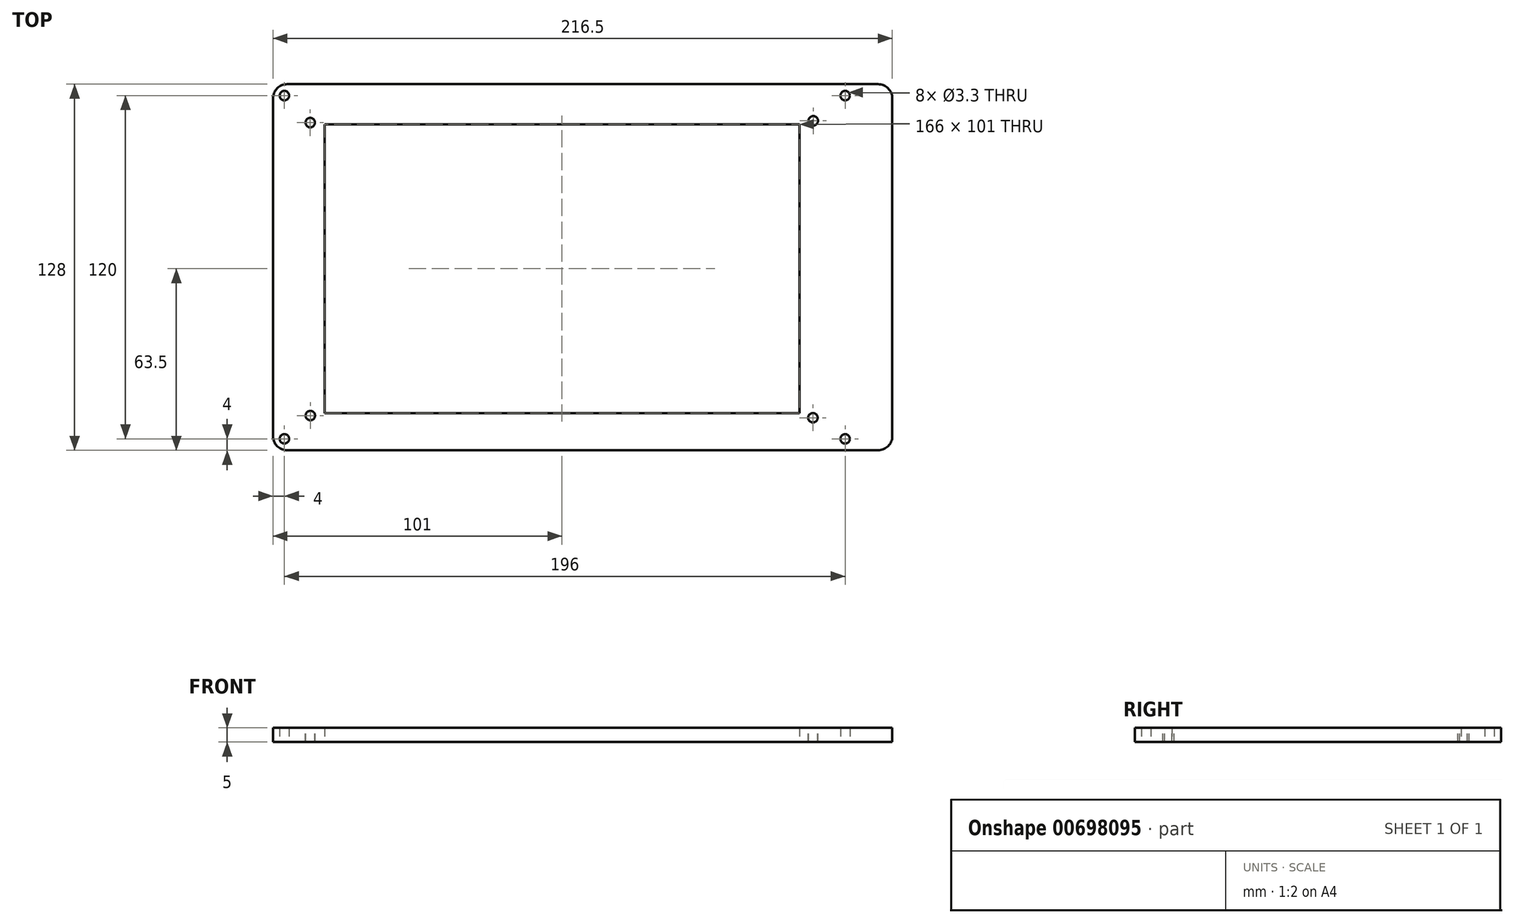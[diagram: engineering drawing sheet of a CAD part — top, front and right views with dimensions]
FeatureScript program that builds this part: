
annotation { "Feature Type Name" : "Feature", "Feature Type Description" : "" }
export const myFeature = defineFeature(function(context is Context, id is Id, definition is map)
    precondition{}
    {
        {
            var Q0;
            Q0=qCreatedBy(makeId("Top.planeOp"),FACE);
            var sketch = newSketch(context, id + "F0", { "sketchPlane" : qUnion([Q0])});
            skLineSegment(sketch, "E0.bottom", {"start": v(83, 50.5) * mm, "end": v(-83, 50.5) * mm});
            skLineSegment(sketch, "E0.top", {"start": v(83, -50.5) * mm, "end": v(-83, -50.5) * mm});
            skLineSegment(sketch, "E0.left", {"start": v(83, 50.5) * mm, "end": v(83, -50.5) * mm});
            skLineSegment(sketch, "E0.right", {"start": v(-83, 50.5) * mm, "end": v(-83, -50.5) * mm});
            skPoint(sketch, "E0.middle", {"position": v(0, 0) * mm});
            skLineSegment(sketch, "E1.0", {"start": v(-91, 54.5) * mm, "end": v(-91, -53.5) * mm, "construction": true});
            skLineSegment(sketch, "E1.1", {"start": v(93, 54.5) * mm, "end": v(-91, 54.5) * mm, "construction": true});
            skLineSegment(sketch, "E1.2", {"start": v(93, 54.5) * mm, "end": v(93, -53.5) * mm, "construction": true});
            skLineSegment(sketch, "E1.3", {"start": v(93, -53.5) * mm, "end": v(-91, -53.5) * mm, "construction": true});
            skLineSegment(sketch, "E2.0", {"start": v(103, 64.5) * mm, "end": v(-101, 64.5) * mm});
            skLineSegment(sketch, "E2.1", {"start": v(103, 64.5) * mm, "end": v(103, -63.5) * mm});
            skLineSegment(sketch, "E2.2", {"start": v(103, -63.5) * mm, "end": v(-101, -63.5) * mm});
            skLineSegment(sketch, "E2.3", {"start": v(-101, 64.5) * mm, "end": v(-101, -63.5) * mm});
            skLineSegment(sketch, "E3.0", {"start": v(99, 60.5) * mm, "end": v(-97, 60.5) * mm, "construction": true});
            skLineSegment(sketch, "E3.1", {"start": v(99, 60.5) * mm, "end": v(99, -59.5) * mm, "construction": true});
            skLineSegment(sketch, "E3.2", {"start": v(99, -59.5) * mm, "end": v(-97, -59.5) * mm, "construction": true});
            skLineSegment(sketch, "E3.3", {"start": v(-97, 60.5) * mm, "end": v(-97, -59.5) * mm, "construction": true});
            skLineSegment(sketch, "E4", {"start": v(103, 64.5) * mm, "end": v(115.5, 64.5) * mm});
            skLineSegment(sketch, "E5", {"start": v(115.5, -63.5) * mm, "end": v(103, -63.5) * mm});
            skLineSegment(sketch, "E6", {"start": v(115.5, 64.5) * mm, "end": v(115.5, -63.5) * mm});
            skPoint(sketch, "E7.orphan", {"position": v(133, -63.5) * mm});
            skSolve(sketch);
        }
        {
            var Q0;
            Q0=makeQuery(id+"F0.imprint","IMPRINT",FACE,{"disambiguationData":[TD([[makeQuery(id+"F0.imprint","IMPRINT",EDGE,{"derivedFrom":sQuery(id+"F0.wireOp",EDGE,"E0.bottom")}),-1.0]])]});
            var Q1;
            Q1=makeQuery(id+"F0.imprint","IMPRINT",FACE,{"disambiguationData":[TD([[makeQuery(id+"F0.imprint","IMPRINT",EDGE,{"derivedFrom":sQuery(id+"F0.wireOp",EDGE,"E2.1")}),1.0]])]});
            extrude(context, id + "F1", {"entities" : qUnion([Q0, Q1]), "depth" : 5 * mm, "offsetDistance" : 25 * mm});
        }
        {
            var Q0;
            Q0=sQuery(id+"F0.wireOp",VERTEX,"E3.0.end");
            var Q1;
            Q1=sQuery(id+"F0.wireOp",VERTEX,"E3.0.start");
            var Q2;
            Q2=sQuery(id+"F0.wireOp",VERTEX,"E3.1.end");
            var Q3;
            Q3=sQuery(id+"F0.wireOp",VERTEX,"E3.2.end");
            var Q4;
            Q4=makeQuery(id+"F1.opExtrude","SWEPT_BODY",BODY,{"disambiguationData":[OSD([sQuery(id+"F0.wireOp",EDGE,"E0.bottom"),sQuery(id+"F0.wireOp",EDGE,"E0.top"),sQuery(id+"F0.wireOp",EDGE,"E0.left"),sQuery(id+"F0.wireOp",EDGE,"E0.right"),sQuery(id+"F0.wireOp",EDGE,"E2.0"),sQuery(id+"F0.wireOp",EDGE,"E2.1"),sQuery(id+"F0.wireOp",EDGE,"E2.2"),sQuery(id+"F0.wireOp",EDGE,"E2.3")])]});
            hole(context, id + "F2", {"style" : HoleStyle.SIMPLE, "endStyle" : HoleEndStyle.THROUGH, "oppositeDirection" : true, "standardTappedOrClearance" : lookupTablePath({ "standard" : "ISO", "fit" : "Normal", "size" : "M3", "type" : "Clearance" }), "standardBlindInLast" : lookupTablePath({ "fit" : "Standard", "standard" : "ISO", "size" : "M3", "type" : "Clearance" }), "holeDiameter" : 3.3 * mm, "majorDiameter" : 5 * mm, "isTappedThrough" : true, "tappedDepth" : 12 * mm, "tapClearance" : 3, "startFromSketch" : true, "locations" : qUnion([Q0, Q1, Q2, Q3]), "scope" : qUnion([Q4])});
        }
        {
            var Q0;
            Q0=makeQuery(id+"F1.opExtrude","CAP_FACE",FACE,{"disambiguationData":[OSD([sQuery(id+"F0.wireOp",EDGE,"E0.bottom"),sQuery(id+"F0.wireOp",EDGE,"E0.top"),sQuery(id+"F0.wireOp",EDGE,"E0.left"),sQuery(id+"F0.wireOp",EDGE,"E0.right"),sQuery(id+"F0.wireOp",EDGE,"E2.0"),sQuery(id+"F0.wireOp",EDGE,"E2.2"),sQuery(id+"F0.wireOp",EDGE,"E2.3"),sQuery(id+"F0.wireOp",EDGE,"E4"),sQuery(id+"F0.wireOp",EDGE,"E5"),sQuery(id+"F0.wireOp",EDGE,"E6")])],"isStart":false});
            var sketch = newSketch(context, id + "F3", { "sketchPlane" : qUnion([Q0])});
            skPoint(sketch, "E8", {"position": v(87.73, -52.12) * mm});
            skPoint(sketch, "E9", {"position": v(-87.92, -51.37) * mm});
            skPoint(sketch, "E10", {"position": v(-87.97, 51.06) * mm});
            skPoint(sketch, "E11", {"position": v(87.85, 51.7) * mm});
            skSolve(sketch);
        }
        {
            var Q0;
            Q0=sQuery(id+"F3.wireOp",VERTEX,"E10");
            var Q1;
            Q1=sQuery(id+"F3.wireOp",VERTEX,"E11");
            var Q2;
            Q2=sQuery(id+"F3.wireOp",VERTEX,"E8");
            var Q3;
            Q3=sQuery(id+"F3.wireOp",VERTEX,"E9");
            var Q4;
            Q4=makeQuery(id+"F1.opExtrude","SWEPT_BODY",BODY,{"disambiguationData":[OSD([sQuery(id+"F0.wireOp",EDGE,"E0.bottom"),sQuery(id+"F0.wireOp",EDGE,"E0.top"),sQuery(id+"F0.wireOp",EDGE,"E0.left"),sQuery(id+"F0.wireOp",EDGE,"E0.right"),sQuery(id+"F0.wireOp",EDGE,"E2.0"),sQuery(id+"F0.wireOp",EDGE,"E2.2"),sQuery(id+"F0.wireOp",EDGE,"E2.3"),sQuery(id+"F0.wireOp",EDGE,"E4"),sQuery(id+"F0.wireOp",EDGE,"E5"),sQuery(id+"F0.wireOp",EDGE,"E6")])]});
            hole(context, id + "F4", {"style" : HoleStyle.SIMPLE, "endStyle" : HoleEndStyle.THROUGH, "standardTappedOrClearance" : lookupTablePath({ "standard" : "ISO", "fit" : "Normal", "size" : "M3", "type" : "Clearance" }), "standardBlindInLast" : lookupTablePath({ "fit" : "Standard", "standard" : "ISO", "size" : "M3", "type" : "Clearance" }), "holeDiameter" : 3.3 * mm, "majorDiameter" : 5 * mm, "isTappedThrough" : true, "tappedDepth" : 12 * mm, "tapClearance" : 3, "locations" : qUnion([Q0, Q1, Q2, Q3]), "scope" : qUnion([Q4])});
        }
        {
            var Q0;
            Q0=makeQuery(id+"F1.opExtrude","SWEPT_EDGE",EDGE,{"disambiguationData":[OSD([sQuery(id+"F0.wireOp",EDGE,"E2.0"),sQuery(id+"F0.wireOp",EDGE,"E2.3")])]});
            var Q1;
            Q1=makeQuery(id+"F1.opExtrude","SWEPT_EDGE",EDGE,{"disambiguationData":[OSD([sQuery(id+"F0.wireOp",EDGE,"E4"),sQuery(id+"F0.wireOp",EDGE,"E6")])]});
            var Q2;
            Q2=makeQuery(id+"F1.opExtrude","SWEPT_EDGE",EDGE,{"disambiguationData":[OSD([sQuery(id+"F0.wireOp",EDGE,"E5"),sQuery(id+"F0.wireOp",EDGE,"E6")])]});
            var Q3;
            Q3=makeQuery(id+"F1.opExtrude","SWEPT_EDGE",EDGE,{"disambiguationData":[OSD([sQuery(id+"F0.wireOp",EDGE,"E2.2"),sQuery(id+"F0.wireOp",EDGE,"E2.3")])]});
            fillet(context, id + "F5", {"entities" : qUnion([Q0, Q1, Q2, Q3]), "radius" : 5 * mm, "tangentPropagation" : true, "allowEdgeOverflow" : false});
        }
    });
